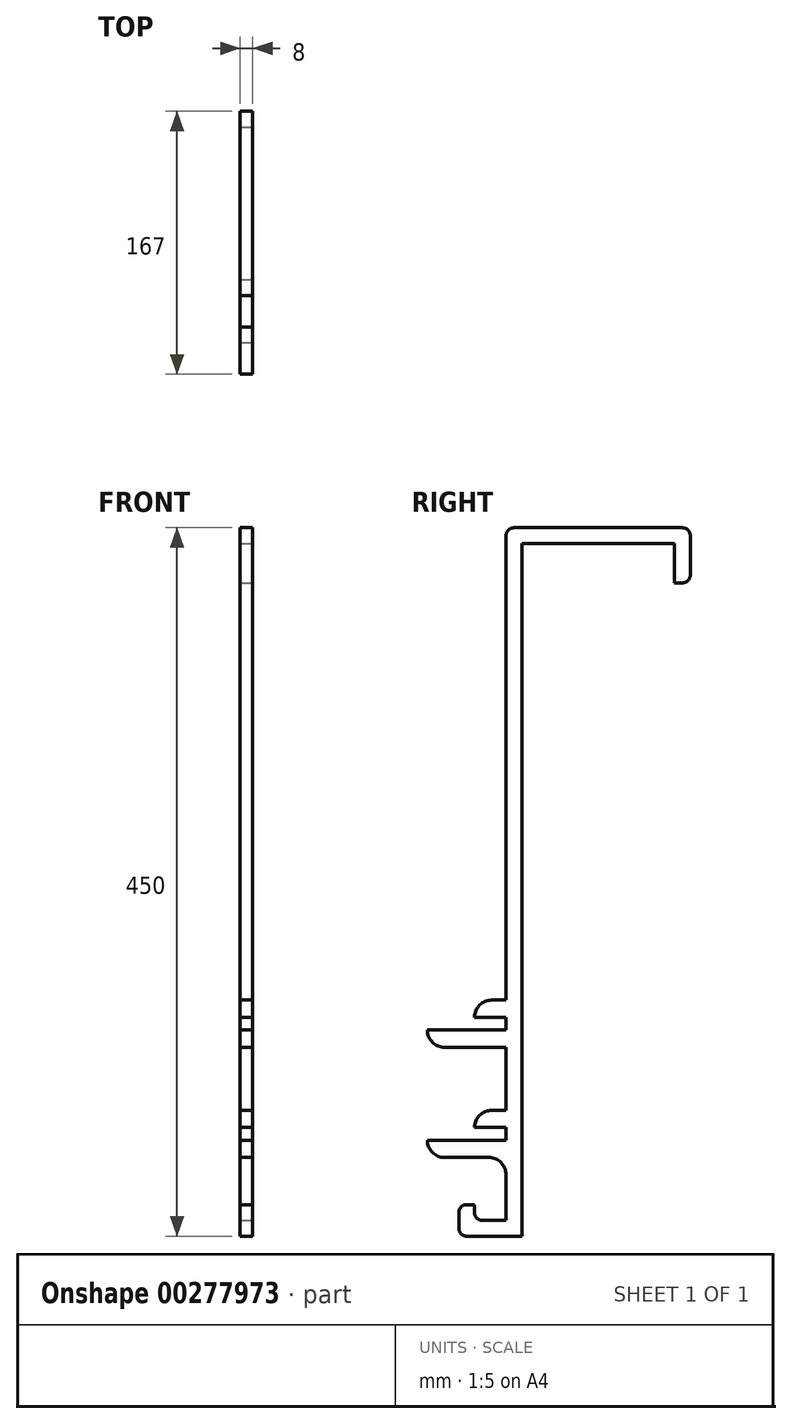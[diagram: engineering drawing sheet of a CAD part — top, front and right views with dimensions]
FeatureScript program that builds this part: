
annotation { "Feature Type Name" : "Feature", "Feature Type Description" : "" }
export const myFeature = defineFeature(function(context is Context, id is Id, definition is map)
    precondition{}
    {
        {
            var Q0;
            Q0=qCreatedBy(makeId("Right.planeOp"),FACE);
            var sketch = newSketch(context, id + "F0", { "sketchPlane" : qUnion([Q0])});
            skLineSegment(sketch, "E0", {"start": v(-1.6, 292.93) * mm, "end": v(-1.6, -7.07) * mm});
            skLineSegment(sketch, "E1", {"start": v(-1.6, -147.07) * mm, "end": v(-21.6, -147.07) * mm});
            skLineSegment(sketch, "E2", {"start": v(-21.6, -147.07) * mm, "end": v(-21.6, -137.07) * mm});
            skLineSegment(sketch, "E3", {"start": v(-21.6, -137.07) * mm, "end": v(-31.6, -137.07) * mm});
            skLineSegment(sketch, "E4", {"start": v(-31.6, -137.07) * mm, "end": v(-31.6, -157.07) * mm});
            skLineSegment(sketch, "E5", {"start": v(-1.6, 292.93) * mm, "end": v(115.4, 292.93) * mm});
            skLineSegment(sketch, "E6", {"start": v(115.4, 292.93) * mm, "end": v(115.4, 257.93) * mm});
            skLineSegment(sketch, "E7", {"start": v(115.4, 257.93) * mm, "end": v(105.4, 257.93) * mm});
            skLineSegment(sketch, "E8", {"start": v(105.4, 257.93) * mm, "end": v(105.4, 282.93) * mm});
            skLineSegment(sketch, "E9", {"start": v(105.4, 282.93) * mm, "end": v(8.4, 282.93) * mm});
            skLineSegment(sketch, "E10", {"start": v(-1.6, -7.07) * mm, "end": v(-21.6, -7.07) * mm});
            skLineSegment(sketch, "E11", {"start": v(-21.6, -7.07) * mm, "end": v(-21.6, -18.07) * mm});
            skLineSegment(sketch, "E12", {"start": v(-21.6, -18.07) * mm, "end": v(-1.6, -18.07) * mm});
            skLineSegment(sketch, "E13", {"start": v(-1.6, -18.07) * mm, "end": v(-1.6, -26.07) * mm});
            skLineSegment(sketch, "E14", {"start": v(-1.6, -26.07) * mm, "end": v(-51.6, -26.07) * mm});
            skLineSegment(sketch, "E15", {"start": v(-51.6, -26.07) * mm, "end": v(-51.6, -37.07) * mm});
            skLineSegment(sketch, "E16", {"start": v(-51.6, -37.07) * mm, "end": v(-1.6, -37.07) * mm});
            skLineSegment(sketch, "E17", {"start": v(-1.6, -37.07) * mm, "end": v(-1.6, -77.07) * mm});
            skLineSegment(sketch, "E18", {"start": v(-1.6, -77.07) * mm, "end": v(-21.6, -77.07) * mm});
            skLineSegment(sketch, "E19", {"start": v(-21.6, -77.07) * mm, "end": v(-21.6, -88.07) * mm});
            skLineSegment(sketch, "E20", {"start": v(-21.6, -88.07) * mm, "end": v(-1.6, -88.07) * mm});
            skLineSegment(sketch, "E21", {"start": v(-1.6, -88.07) * mm, "end": v(-1.6, -96.07) * mm});
            skLineSegment(sketch, "E22", {"start": v(-1.6, -96.07) * mm, "end": v(-51.6, -96.07) * mm});
            skLineSegment(sketch, "E23", {"start": v(-51.6, -107.07) * mm, "end": v(-1.6, -107.07) * mm});
            skLineSegment(sketch, "E24", {"start": v(-1.6, -107.07) * mm, "end": v(-1.6, -147.07) * mm});
            skLineSegment(sketch, "E25", {"start": v(-31.6, -157.07) * mm, "end": v(8.4, -157.07) * mm});
            skLineSegment(sketch, "E26", {"start": v(8.4, -157.07) * mm, "end": v(8.4, 282.93) * mm});
            skLineSegment(sketch, "E27", {"start": v(-51.6, -96.07) * mm, "end": v(-51.6, -107.07) * mm});
            skSolve(sketch);
        }
        {
            var Q0;
            Q0=qSketchRegion(id+"F0",true);
            extrude(context, id + "F1", {"entities" : qUnion([Q0]), "oppositeDirection" : true, "depth" : 8 * mm});
        }
        {
            var Q0;
            Q0=makeQuery(id+"F1.opExtrude","SWEPT_EDGE",EDGE,{"disambiguationData":[OSD([sQuery(id+"F0.wireOp",EDGE,"E15"),sQuery(id+"F0.wireOp",EDGE,"E16")])]});
            fillet(context, id + "F2", {"entities" : qUnion([Q0]), "radius" : 11 * mm, "tangentPropagation" : true, "allowEdgeOverflow" : false});
        }
        {
            var Q0;
            Q0=makeQuery(id+"F1.opExtrude","SWEPT_EDGE",EDGE,{"disambiguationData":[OSD([sQuery(id+"F0.wireOp",EDGE,"E10"),sQuery(id+"F0.wireOp",EDGE,"E11")])]});
            fillet(context, id + "F3", {"entities" : qUnion([Q0]), "radius" : 11 * mm, "tangentPropagation" : true, "allowEdgeOverflow" : false});
        }
        {
            var Q0;
            Q0=makeQuery(id+"F1.opExtrude","SWEPT_EDGE",EDGE,{"disambiguationData":[OSD([sQuery(id+"F0.wireOp",EDGE,"E18"),sQuery(id+"F0.wireOp",EDGE,"E19")])]});
            fillet(context, id + "F4", {"entities" : qUnion([Q0]), "radius" : 11 * mm, "tangentPropagation" : true, "allowEdgeOverflow" : false});
        }
        {
            var Q0;
            Q0=makeQuery(id+"F1.opExtrude","SWEPT_EDGE",EDGE,{"disambiguationData":[OSD([sQuery(id+"F0.wireOp",EDGE,"ftelP5rY-JesT-e7Vt-sxIh-GGNbXWCKo9JN"),sQuery(id+"F0.wireOp",EDGE,"E23")])]});
            fillet(context, id + "F5", {"entities" : qUnion([Q0]), "radius" : 11 * mm, "tangentPropagation" : true, "allowEdgeOverflow" : false});
        }
        {
            var Q0;
            Q0=makeQuery(id+"F1.opExtrude","SWEPT_EDGE",EDGE,{"disambiguationData":[OSD([sQuery(id+"F0.wireOp",EDGE,"E3"),sQuery(id+"F0.wireOp",EDGE,"E4")])]});
            var Q1;
            Q1=makeQuery(id+"F1.opExtrude","SWEPT_EDGE",EDGE,{"disambiguationData":[OSD([sQuery(id+"F0.wireOp",EDGE,"E4"),sQuery(id+"F0.wireOp",EDGE,"E25")])]});
            var Q2;
            Q2=makeQuery(id+"F1.opExtrude","SWEPT_EDGE",EDGE,{"disambiguationData":[OSD([sQuery(id+"F0.wireOp",EDGE,"E1"),sQuery(id+"F0.wireOp",EDGE,"E2")])]});
            fillet(context, id + "F6", {"entities" : qUnion([Q0, Q1, Q2]), "radius" : 5 * mm, "tangentPropagation" : true, "allowEdgeOverflow" : false});
        }
        {
            var Q0;
            Q0=makeQuery(id+"F1.opExtrude","SWEPT_EDGE",EDGE,{"disambiguationData":[OSD([sQuery(id+"F0.wireOp",EDGE,"E0"),sQuery(id+"F0.wireOp",EDGE,"E5")])]});
            var Q1;
            Q1=makeQuery(id+"F1.opExtrude","SWEPT_EDGE",EDGE,{"disambiguationData":[OSD([sQuery(id+"F0.wireOp",EDGE,"E5"),sQuery(id+"F0.wireOp",EDGE,"E6")])]});
            var Q2;
            Q2=makeQuery(id+"F1.opExtrude","SWEPT_EDGE",EDGE,{"disambiguationData":[OSD([sQuery(id+"F0.wireOp",EDGE,"E6"),sQuery(id+"F0.wireOp",EDGE,"E7")])]});
            fillet(context, id + "F7", {"entities" : qUnion([Q0, Q1, Q2]), "radius" : 5 * mm, "tangentPropagation" : true, "allowEdgeOverflow" : false});
        }
    });
